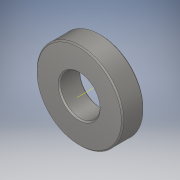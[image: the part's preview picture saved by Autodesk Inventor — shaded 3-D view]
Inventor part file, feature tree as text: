
AUTODESK INVENTOR PART (.ipt)
format: ipt  version: 2019.4 (Build 234330000, 330)  size: 122,368 bytes
history: native  units: in
note: dims shown in document units (in); Inventor stores cm internally (conversion verified against a paired STEP export)
features: plane x2, extrude x1, chamfer x1, sketch x1
ambient origin geometry x8: Origin, YZ Plane, XZ Plane, XY Plane, X Axis, Y Axis, Z Axis, Center Point
bodies: Solid1 (feature_tree)
feature tree (5):
  extrude  "Extrusion1"  Depth=0.3438in TaperAngle=45.0deg
  chamfer  "Chamfer1"  Distance=0.625in
  plane  "Work Plane1"
  plane  "Work Plane2"
  sketch  "Sketch1"  dims[d2=0.3438in d3=0.0in d4=0.02in d5=0.125in d6=45.0deg d7=0.625in d8=1.375in]
